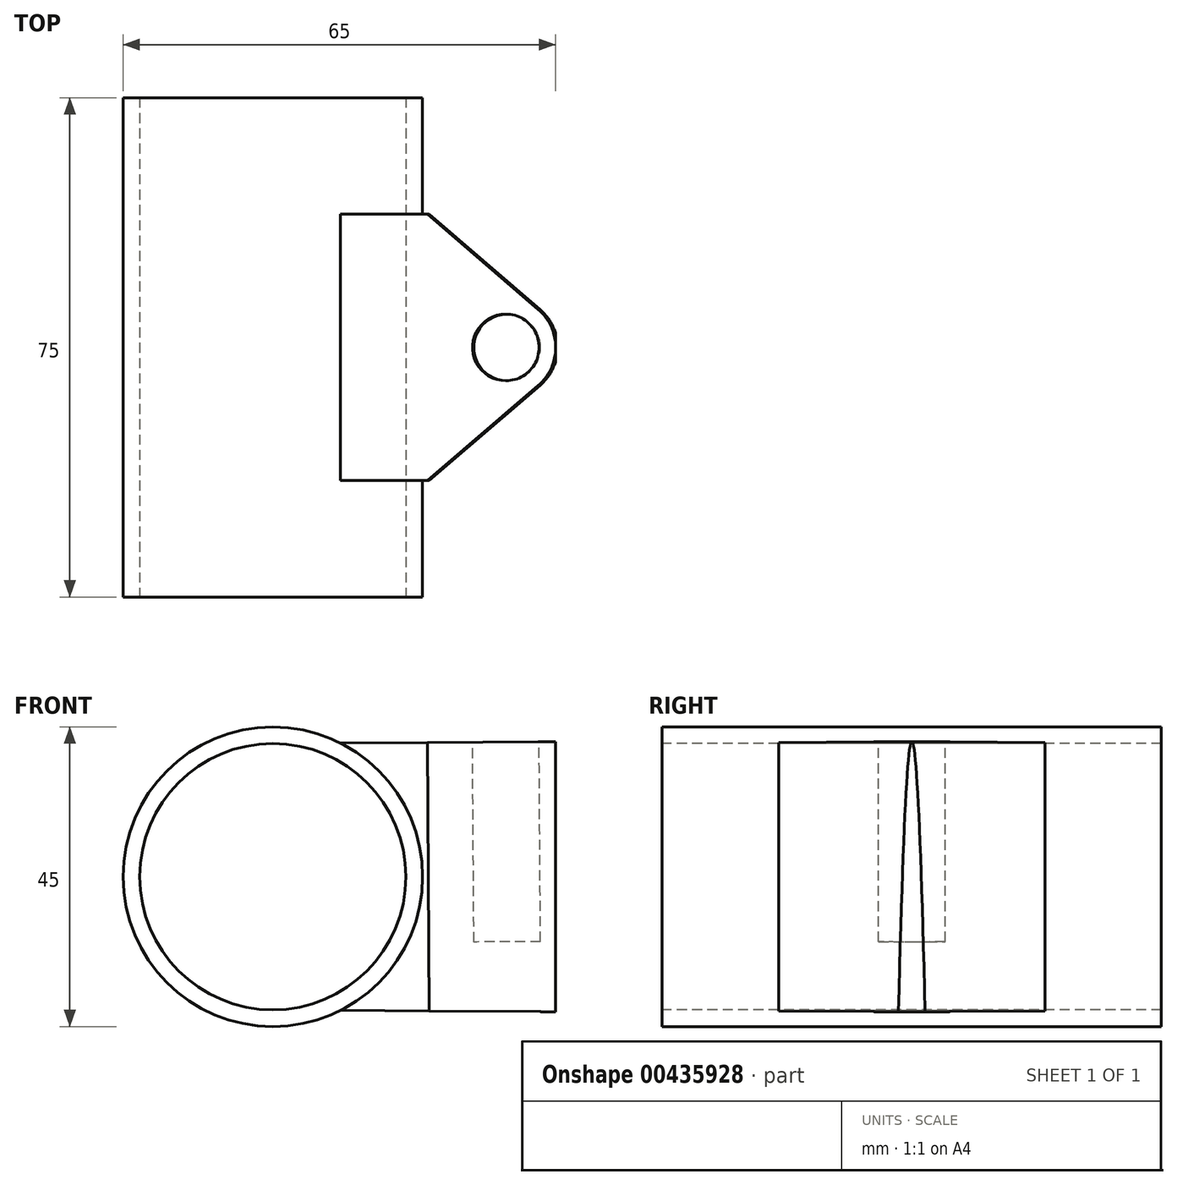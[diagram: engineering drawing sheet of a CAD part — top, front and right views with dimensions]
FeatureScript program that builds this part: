
annotation { "Feature Type Name" : "Feature", "Feature Type Description" : "" }
export const myFeature = defineFeature(function(context is Context, id is Id, definition is map)
    precondition{}
    {
        {
            var Q0;
            Q0=qCreatedBy(makeId("Front.planeOp"),FACE);
            var sketch = newSketch(context, id + "F0", { "sketchPlane" : qUnion([Q0])});
            skPoint(sketch, "E0.middle", {"position": v(0, 0) * mm});
            skCircle(sketch, "E1", {"center": v(0, 0) * mm, "radius": 22.5 * mm});
            skLineSegment(sketch, "E2", {"start": v(42.5, 0) * mm, "end": v(42.5, -20.29) * mm});
            skLineSegment(sketch, "E3", {"start": v(42.5, -20.29) * mm, "end": v(10.17, -20.07) * mm});
            skLineSegment(sketch, "E4", {"start": v(42.5, 0) * mm, "end": v(42.5, 20.29) * mm});
            skLineSegment(sketch, "E5", {"start": v(42.5, 20.29) * mm, "end": v(10.17, 20.07) * mm});
            skSolve(sketch);
        }
        {
            var Q0;
            {var subQ0=sQuery(id+"F0.wireOp",EDGE,"E1");var subQ1=makeQuery(id+"F0.imprint","INTERSECT",VERTEX,{"derivedFrom":[subQ0,sQuery(id+"F0.wireOp",EDGE,"E3")]});Q0=makeQuery(id+"F0.imprint","IMPRINT",FACE,{"disambiguationData":[TD([[makeQuery(id+"F0.imprint","IMPRINT",EDGE,{"disambiguationData":[TD([[subQ1,1.0]])],"derivedFrom":subQ0}),1.0]])]});}
            extrude(context, id + "F1", {"entities" : qUnion([Q0]), "endBound" : BoundingType.SYMMETRIC, "depth" : 75 * mm});
        }
        {
            var Q0;
            Q0=makeQuery(id+"F0.imprint","IMPRINT",FACE,{"disambiguationData":[TD([[makeQuery(id+"F0.imprint","IMPRINT",EDGE,{"derivedFrom":sQuery(id+"F0.wireOp",EDGE,"E2")}),-1.0]])]});
            extrude(context, id + "F2", {"entities" : qUnion([Q0]), "operationType" : NewBodyOperationType.ADD, "endBound" : BoundingType.SYMMETRIC, "depth" : 40 * mm});
        }
        {
            var Q0;
            Q0=makeQuery(id+"F2.opExtrude","SWEPT_FACE",FACE,{"disambiguationData":[OSD([sQuery(id+"F0.wireOp",EDGE,"E5")])]});
            var sketch = newSketch(context, id + "F3", { "sketchPlane" : qUnion([Q0])});
            skPoint(sketch, "E6.endSnap0", {"position": v(42.64, 0) * mm});
            skCircle(sketch, "E7", {"center": v(35.14, 0) * mm, "radius": 7.5 * mm});
            skLineSegment(sketch, "E8", {"start": v(23.36, 20) * mm, "end": v(23.36, -20) * mm});
            skPoint(sketch, "E8.endSnap0", {"position": v(26.47, -20) * mm});
            skLineSegment(sketch, "E9", {"start": v(23.36, 20) * mm, "end": v(35.14, 7.5) * mm});
            skLineSegment(sketch, "E10", {"start": v(35.14, -7.5) * mm, "end": v(23.36, -20) * mm});
            skLineSegment(sketch, "E11", {"start": v(23.36, 20) * mm, "end": v(40.02, 5.69) * mm});
            skLineSegment(sketch, "E12", {"start": v(40.02, -5.69) * mm, "end": v(23.36, -20) * mm});
            skCircle(sketch, "E13", {"center": v(35.14, 0) * mm, "radius": 5 * mm});
            skSolve(sketch);
        }
        {
            var Q0;
            {var subQ0=sQuery(id+"F3.wireOp",EDGE,"E11");Q0=makeQuery(id+"F3.imprint","IMPRINT",FACE,{"disambiguationData":[TD([[makeQuery(id+"F3.imprint","IMPRINT",EDGE,{"derivedFrom":subQ0}),1.0]])]});}
            var Q1;
            {var subQ0=sQuery(id+"F3.wireOp",EDGE,"E12");Q1=makeQuery(id+"F3.imprint","IMPRINT",FACE,{"disambiguationData":[TD([[makeQuery(id+"F3.imprint","IMPRINT",EDGE,{"derivedFrom":subQ0}),1.0]])]});}
            extrude(context, id + "F4", {"entities" : qUnion([Q0, Q1]), "operationType" : NewBodyOperationType.REMOVE, "oppositeDirection" : true, "depth" : 70 * mm});
        }
        {
            var Q0;
            Q0=makeQuery(id+"F3.imprint","IMPRINT",FACE,{"disambiguationData":[TD([[makeQuery(id+"F3.imprint","IMPRINT",EDGE,{"derivedFrom":sQuery(id+"F3.wireOp",EDGE,"E13")}),1.0]])]});
            extrude(context, id + "F5", {"entities" : qUnion([Q0]), "operationType" : NewBodyOperationType.REMOVE, "oppositeDirection" : true, "depth" : 30 * mm});
        }
        {
            var Q0;
            Q0=makeQuery(id+"F1.opExtrude","CAP_FACE",FACE,{"disambiguationData":[OSD([sQuery(id+"F0.wireOp",EDGE,"E1")])],"isStart":false});
            var sketch = newSketch(context, id + "F6", { "sketchPlane" : qUnion([Q0])});
            skCircle(sketch, "E14", {"center": v(0, 0) * mm, "radius": 20 * mm});
            skSolve(sketch);
        }
        {
            var Q0;
            Q0=makeQuery(id+"F6.imprint","IMPRINT",FACE,{"disambiguationData":[TD([[makeQuery(id+"F6.imprint","IMPRINT",EDGE,{"derivedFrom":sQuery(id+"F6.wireOp",EDGE,"E14")}),1.0]])]});
            extrude(context, id + "F7", {"entities" : qUnion([Q0]), "operationType" : NewBodyOperationType.REMOVE, "oppositeDirection" : true, "depth" : 100 * mm});
        }
    });
